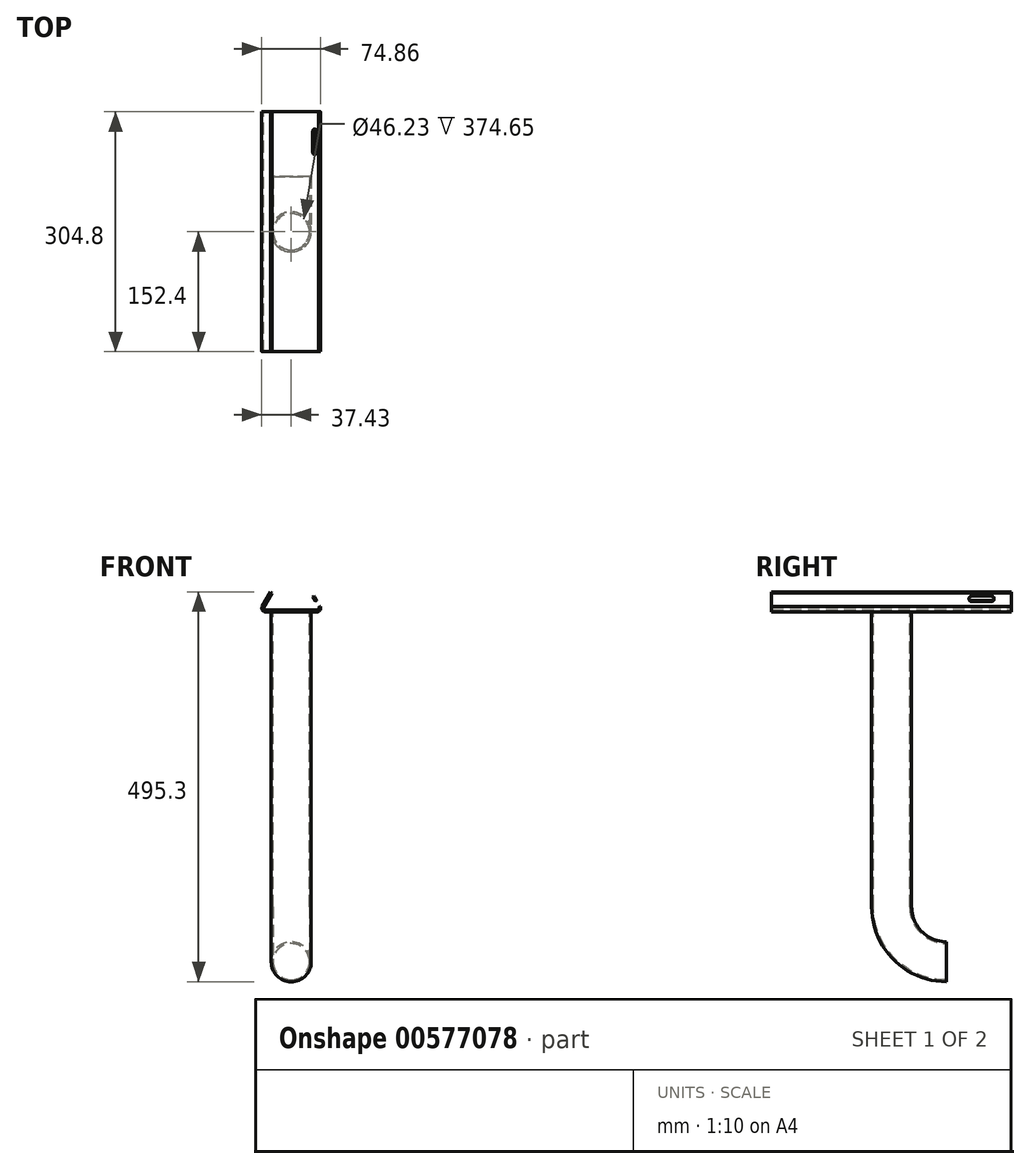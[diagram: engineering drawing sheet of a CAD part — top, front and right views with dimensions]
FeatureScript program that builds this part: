
annotation { "Feature Type Name" : "Feature", "Feature Type Description" : "" }
export const myFeature = defineFeature(function(context is Context, id is Id, definition is map)
    precondition{}
    {
        {
            var Q0;
            Q0=qCreatedBy(makeId("Front.planeOp"),FACE);
            var sketch = newSketch(context, id + "F0", { "sketchPlane" : qUnion([Q0])});
            skLineSegment(sketch, "E0", {"start": v(-32.86, 0) * mm, "end": v(32.86, 0) * mm});
            skLineSegment(sketch, "E1", {"start": v(36.81, 6.86) * mm, "end": v(26.1, 25.4) * mm});
            skLineSegment(sketch, "E2", {"start": v(-36.81, 6.86) * mm, "end": v(-26.1, 25.4) * mm});
            skLineSegment(sketch, "E3", {"start": v(0, 44.5) * mm, "end": v(0, -47.28) * mm, "construction": true});
            skLineSegment(sketch, "E4.0", {"start": v(-32.86, 2.29) * mm, "end": v(32.86, 2.29) * mm});
            skLineSegment(sketch, "E5.0", {"start": v(-34.84, 5.71) * mm, "end": v(-24.13, 24.26) * mm});
            skLineSegment(sketch, "E6.0", {"start": v(34.84, 5.71) * mm, "end": v(24.13, 24.26) * mm});
            skLineSegment(sketch, "E7", {"start": v(-26.1, 25.4) * mm, "end": v(-24.13, 24.26) * mm});
            skLineSegment(sketch, "E8", {"start": v(24.13, 24.26) * mm, "end": v(26.1, 25.4) * mm});
            skPoint(sketch, "E9.visualSharp", {"position": v(-36.81, 2.29) * mm});
            skArc(sketch, "E9.filletArc", {"start": v(-34.84, 5.72) * mm, "mid": v(-34.84, 3.43) * mm, "end": v(-32.86, 2.29) * mm});
            skPoint(sketch, "E10.visualSharp", {"position": v(36.81, 2.29) * mm});
            skArc(sketch, "E10.filletArc", {"start": v(32.86, 2.29) * mm, "mid": v(34.84, 3.43) * mm, "end": v(34.84, 5.72) * mm});
            skPoint(sketch, "E11.visualSharp", {"position": v(-40.77, 0) * mm});
            skArc(sketch, "E11.filletArc", {"start": v(-36.81, 6.86) * mm, "mid": v(-36.81, 2.29) * mm, "end": v(-32.86, 0) * mm});
            skPoint(sketch, "E12.visualSharp", {"position": v(40.77, 0) * mm});
            skArc(sketch, "E12.filletArc", {"start": v(32.86, 0) * mm, "mid": v(36.81, 2.29) * mm, "end": v(36.81, 6.86) * mm});
            skSolve(sketch);
        }
        {
            var Q0;
            Q0=makeQuery(id+"F0.imprint","IMPRINT",FACE,{"disambiguationData":[TD([[makeQuery(id+"F0.imprint","IMPRINT",EDGE,{"derivedFrom":sQuery(id+"F0.wireOp",EDGE,"E0")}),1.0]])]});
            extrude(context, id + "F1", {"entities" : qUnion([Q0]), "depth" : 304.8 * mm});
        }
        {
            var Q0;
            Q0=makeQuery(id+"F1.opExtrude","CAP_FACE",FACE,{"disambiguationData":[OSD([sQuery(id+"F0.wireOp",EDGE,"E0"),sQuery(id+"F0.wireOp",EDGE,"E1"),sQuery(id+"F0.wireOp",EDGE,"E2"),sQuery(id+"F0.wireOp",EDGE,"E4.0"),sQuery(id+"F0.wireOp",EDGE,"E5.0"),sQuery(id+"F0.wireOp",EDGE,"E6.0"),sQuery(id+"F0.wireOp",EDGE,"E7"),sQuery(id+"F0.wireOp",EDGE,"E8"),sQuery(id+"F0.wireOp",EDGE,"E9.filletArc"),sQuery(id+"F0.wireOp",EDGE,"E10.filletArc"),sQuery(id+"F0.wireOp",EDGE,"E11.filletArc"),sQuery(id+"F0.wireOp",EDGE,"E12.filletArc")])],"isStart":false});
            cPlane(context, id + "F2", {"entities" : qUnion([Q0]), "cplaneType" : CPlaneType.OFFSET, "offset" : 152.4 * mm, "oppositeDirection" : true, "width" : 152.4 * mm, "height" : 152.4 * mm});
        }
        {
            var Q0;
            Q0=qCreatedBy(makeId("Right.planeOp"),FACE);
            var sketch = newSketch(context, id + "F3", { "sketchPlane" : qUnion([Q0])});
            skLineSegment(sketch, "E13", {"start": v(-152.4, 0) * mm, "end": v(-152.4, -374.65) * mm});
            skLineSegment(sketch, "E14.0", {"start": v(-304.8, -444.5) * mm, "end": v(0, -444.5) * mm, "construction": true});
            skArc(sketch, "E15", {"start": v(-152.4, -374.65) * mm, "mid": v(-131.94, -424.04) * mm, "end": v(-82.55, -444.5) * mm});
            skPoint(sketch, "E15.first.point", {"position": v(-152.4, -374.65) * mm});
            skPoint(sketch, "E15.second.point", {"position": v(-82.55, -444.5) * mm});
            skPoint(sketch, "E15.third.point", {"position": v(-82.55, -444.5) * mm});
            skSolve(sketch);
        }
        {
            var Q0;
            Q0=sQuery(id+"F3.wireOp",VERTEX,"E15.third.point");
            var Q1;
            Q1=qCreatedBy(makeId("Front.planeOp"),FACE);
            cPlane(context, id + "F4", {"entities" : qUnion([Q0, Q1]), "cplaneType" : CPlaneType.PLANE_POINT, "offset" : 25.4 * mm, "width" : 152.4 * mm, "height" : 152.4 * mm});
        }
        {
            var Q0;
            Q0=qCreatedBy(id+"F4.planeOp",FACE);
            var sketch = newSketch(context, id + "F5", { "sketchPlane" : qUnion([Q0])});
            skCircle(sketch, "E16", {"center": v(0, -444.5) * mm, "radius": 25.4 * mm});
            skCircle(sketch, "E17", {"center": v(0, -444.5) * mm, "radius": 23.11 * mm});
            skSolve(sketch);
        }
        {
            var Q0;
            Q0=qSketchRegion(id+"F5",true);
            var Q1;
            Q1=qConstructionFilter(qBodyType(qCreatedBy(id+"F3",EDGE),BodyType.WIRE),ConstructionObject.NO);
            sweep(context, id + "F6", {"operationType" : NewBodyOperationType.ADD, "profiles" : qUnion([Q0]), "path" : qUnion([Q1])});
        }
        {
            var Q0;
            Q0=makeQuery(id+"F1.opExtrude","SWEPT_FACE",FACE,{"disambiguationData":[OSD([sQuery(id+"F0.wireOp",EDGE,"E1")])]});
            var sketch = newSketch(context, id + "F7", { "sketchPlane" : qUnion([Q0])});
            skArc(sketch, "E18", {"start": v(-279.4, 2.6) * mm, "mid": v(-282.58, -0.58) * mm, "end": v(-279.4, -3.76) * mm});
            skArc(sketch, "E19", {"start": v(-254, -3.76) * mm, "mid": v(-250.83, -0.58) * mm, "end": v(-254, 2.6) * mm});
            skLineSegment(sketch, "E20", {"start": v(-279.4, 2.6) * mm, "end": v(-254, 2.6) * mm});
            skLineSegment(sketch, "E21", {"start": v(-279.4, -3.76) * mm, "end": v(-254, -3.76) * mm});
            skLineSegment(sketch, "E22", {"start": v(-152.4, 93.04) * mm, "end": v(-152.4, -99.81) * mm, "construction": true});
            skPoint(sketch, "E22.startSnap0", {"position": v(-152.4, -12.47) * mm});
            skArc(sketch, "E23.MirrorCS", {"start": v(-25.4, 2.6) * mm, "mid": v(-22.23, -0.58) * mm, "end": v(-25.4, -3.76) * mm});
            skLineSegment(sketch, "E24.MirrorCS", {"start": v(-25.4, 2.6) * mm, "end": v(-50.8, 2.6) * mm});
            skArc(sketch, "E25.MirrorCS", {"start": v(-50.8, -3.76) * mm, "mid": v(-53.98, -0.58) * mm, "end": v(-50.8, 2.6) * mm});
            skLineSegment(sketch, "E26.MirrorCS", {"start": v(-25.4, -3.76) * mm, "end": v(-50.8, -3.76) * mm});
            skArc(sketch, "E27", {"start": v(-165.1, 2.6) * mm, "mid": v(-168.28, -0.58) * mm, "end": v(-165.1, -3.76) * mm});
            skArc(sketch, "E28", {"start": v(-139.7, -3.76) * mm, "mid": v(-136.53, -0.58) * mm, "end": v(-139.7, 2.6) * mm});
            skLineSegment(sketch, "E29", {"start": v(-165.1, 2.6) * mm, "end": v(-139.7, 2.6) * mm});
            skLineSegment(sketch, "E30", {"start": v(-165.1, -3.76) * mm, "end": v(-139.7, -3.76) * mm});
            skSolve(sketch);
        }
        {
            var Q0;
            Q0=makeQuery(id+"F7.imprint","IMPRINT",FACE,{"disambiguationData":[TD([[makeQuery(id+"F7.imprint","IMPRINT",EDGE,{"derivedFrom":sQuery(id+"F7.wireOp",EDGE,"E18")}),1.0]])]});
            var Q1;
            Q1=makeQuery(id+"F7.imprint","IMPRINT",FACE,{"disambiguationData":[TD([[makeQuery(id+"F7.imprint","IMPRINT",EDGE,{"derivedFrom":sQuery(id+"F7.wireOp",EDGE,"E27")}),1.0]])]});
            var Q2;
            Q2=makeQuery(id+"F7.imprint","IMPRINT",FACE,{"disambiguationData":[TD([[makeQuery(id+"F7.imprint","IMPRINT",EDGE,{"derivedFrom":sQuery(id+"F7.wireOp",EDGE,"E23.MirrorCS")}),-1.0]])]});
            extrude(context, id + "F8", {"entities" : qUnion([Q0, Q1, Q2]), "operationType" : NewBodyOperationType.REMOVE, "endBound" : BoundingType.UP_TO_NEXT, "oppositeDirection" : true, "depth" : 25.4 * mm});
        }
    });
